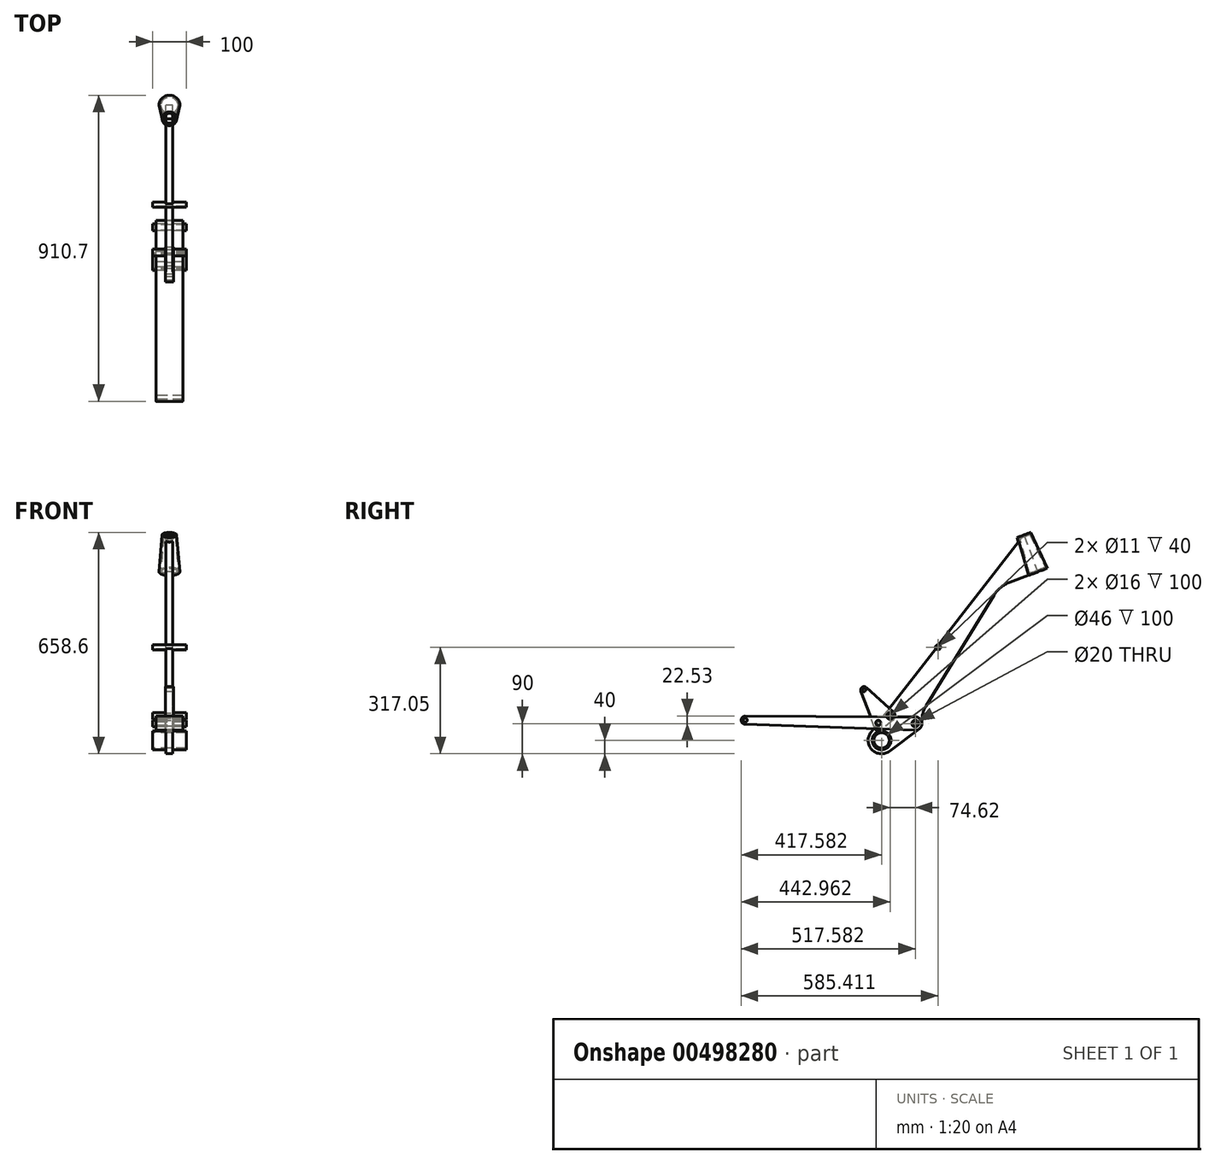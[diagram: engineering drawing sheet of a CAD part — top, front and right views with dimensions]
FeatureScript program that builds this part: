
annotation { "Feature Type Name" : "Feature", "Feature Type Description" : "" }
export const myFeature = defineFeature(function(context is Context, id is Id, definition is map)
    precondition{}
    {
        {
            var Q0;
            Q0=qCreatedBy(makeId("Right.planeOp"),FACE);
            var sketch = newSketch(context, id + "F0", { "sketchPlane" : qUnion([Q0])});
            skLineSegment(sketch, "E0", {"start": v(0, 0) * mm, "end": v(-83.68, 223.8) * mm, "construction": true});
            skLineSegment(sketch, "E1", {"start": v(-295.85, 645.65) * mm, "end": v(-16.13, -102.49) * mm, "construction": true});
            skPoint(sketch, "E2", {"position": v(-219.37, 441.1) * mm});
            skLineSegment(sketch, "E3", {"start": v(-285.85, 416.25) * mm, "end": v(-152.9, 465.96) * mm, "construction": true});
            skCircle(sketch, "E4", {"center": v(0, -8.13) * mm, "radius": 375.7 * mm, "construction": true});
            skPoint(sketch, "E5", {"position": v(-260.46, 551) * mm});
            skPoint(sketch, "E6", {"position": v(-683.46, -60) * mm});
            skPoint(sketch, "E7", {"position": v(-1089.04, 0) * mm});
            skLineSegment(sketch, "E8", {"start": v(-1089.04, 0) * mm, "end": v(0, 0) * mm, "construction": true});
            skCircle(sketch, "E9", {"center": v(-1089.04, 0) * mm, "radius": 375.7 * mm, "construction": true});
            skLineSegment(sketch, "E10", {"start": v(-683.46, -60) * mm, "end": v(-904.4, 662.68) * mm, "construction": true});
            skLineSegment(sketch, "E11", {"start": v(-260.46, 551) * mm, "end": v(-947.84, 551) * mm, "construction": true});
            skPoint(sketch, "E12", {"position": v(-870.26, 551) * mm});
            skLineSegment(sketch, "E13", {"start": v(-207.61, 570.76) * mm, "end": v(-313.3, 531.24) * mm, "construction": true});
            skPoint(sketch, "E14", {"position": v(-249.95, 522.9) * mm});
            skLineSegment(sketch, "E15", {"start": v(-683.46, -60) * mm, "end": v(-249.95, 522.9) * mm, "construction": true});
            skPoint(sketch, "E16", {"position": v(-785.79, 274.7) * mm});
            skLineSegment(sketch, "E17", {"start": v(-785.79, 274.7) * mm, "end": v(-249.95, 522.9) * mm, "construction": true});
            skPoint(sketch, "E18", {"position": v(-517.87, 398.8) * mm});
            skSolve(sketch);
        }
        {
            var Q0;
            Q0=qCreatedBy(makeId("Right.planeOp"),FACE);
            var sketch = newSketch(context, id + "F1", { "sketchPlane" : qUnion([Q0])});
            skLineSegment(sketch, "E19", {"start": v(-243.73, 432) * mm, "end": v(-245.48, 436.69) * mm});
            skLineSegment(sketch, "E20", {"start": v(-275.1, 540.19) * mm, "end": v(-245.48, 436.69) * mm});
            skLineSegment(sketch, "E21", {"start": v(-275.1, 540.19) * mm, "end": v(-276.85, 544.87) * mm});
            skLineSegment(sketch, "E22", {"start": v(-276.85, 544.87) * mm, "end": v(-280.8, 543.4) * mm});
            skLineSegment(sketch, "E23", {"start": v(-280.8, 543.4) * mm, "end": v(-248.4, 430.25) * mm});
            skLineSegment(sketch, "E24", {"start": v(-248.4, 430.25) * mm, "end": v(-243.73, 432) * mm});
            skSolve(sketch);
        }
        {
            var Q0;
            Q0=qSketchRegion(id+"F1",true);
            var Q1;
            Q1=sQuery(id+"F0.wireOp",EDGE,"E1");
            revolve(context, id + "F2", {"entities" : qUnion([Q0]), "axis" : qUnion([Q1]), "revolveType" : RevolveType.FULL});
        }
        {
            var Q0;
            Q0=qCreatedBy(makeId("Right.planeOp"),FACE);
            var sketch = newSketch(context, id + "F3", { "sketchPlane" : qUnion([Q0])});
            skCircle(sketch, "E25", {"center": v(-683.46, -60) * mm, "radius": 23 * mm});
            skCircle(sketch, "E26", {"center": v(-683.46, -60) * mm, "radius": 28 * mm});
            skSolve(sketch);
        }
        {
            var Q0;
            Q0=qSketchRegion(id+"F3",true);
            extrude(context, id + "F4", {"entities" : qUnion([Q0]), "operationType" : NewBodyOperationType.ADD, "endBound" : BoundingType.SYMMETRIC, "depth" : 100 * mm});
        }
        {
            var Q0;
            Q0=qCreatedBy(makeId("Right.planeOp"),FACE);
            var sketch = newSketch(context, id + "F5", { "sketchPlane" : qUnion([Q0])});
            skPoint(sketch, "E27", {"position": v(-583.46, -10) * mm});
            skPoint(sketch, "E28", {"position": v(-658.08, 12.53) * mm});
            skPoint(sketch, "E29", {"position": v(-515.63, 217.05) * mm});
            skSolve(sketch);
        }
        {
            var Q0;
            Q0=qCreatedBy(makeId("Right.planeOp"),FACE);
            var sketch = newSketch(context, id + "F6", { "sketchPlane" : qUnion([Q0])});
            skLineSegment(sketch, "E30", {"start": v(-715.07, -35.5) * mm, "end": v(-489.57, 255.43) * mm});
            skArc(sketch, "E31", {"start": v(-715.07, -35.5) * mm, "mid": v(-711.97, -88.06) * mm, "end": v(-659.46, -92) * mm});
            skLineSegment(sketch, "E32", {"start": v(-550.82, 43.19) * mm, "end": v(-348.97, 372.18) * mm});
            skLineSegment(sketch, "E33", {"start": v(-303.46, 409.67) * mm, "end": v(-219.37, 441.1) * mm});
            skLineSegment(sketch, "E34", {"start": v(-260.46, 551) * mm, "end": v(-219.37, 441.1) * mm});
            skArc(sketch, "E35", {"start": v(-303.46, 409.67) * mm, "mid": v(-329.35, 394.73) * mm, "end": v(-348.97, 372.18) * mm});
            skCircle(sketch, "E36", {"center": v(-683.46, -60) * mm, "radius": 28 * mm});
            skLineSegment(sketch, "E37", {"start": v(-659.46, -92) * mm, "end": v(-571.46, -26) * mm});
            skArc(sketch, "E38", {"start": v(-571.46, -26) * mm, "mid": v(-565.27, -18.31) * mm, "end": v(-563.5, -8.6) * mm});
            skArc(sketch, "E39", {"start": v(-546.3, 182.24) * mm, "mid": v(-478.96, 188.63) * mm, "end": v(-489.57, 255.43) * mm});
            skLineSegment(sketch, "E40.trimOffspring", {"start": v(-546.3, 182.24) * mm, "end": v(-260.46, 551) * mm});
            skArc(sketch, "E41", {"start": v(-550.82, 43.19) * mm, "mid": v(-561.21, 18.28) * mm, "end": v(-563.5, -8.6) * mm});
            skCircle(sketch, "E42", {"center": v(-658.08, 12.53) * mm, "radius": 10 * mm});
            skCircle(sketch, "E43", {"center": v(-583.46, -10) * mm, "radius": 10 * mm});
            skCircle(sketch, "E44", {"center": v(-515.63, 217.05) * mm, "radius": 7.5 * mm});
            skSolve(sketch);
        }
        {
            var Q0;
            Q0=qSketchRegion(id+"F6",true);
            extrude(context, id + "F7", {"entities" : qUnion([Q0]), "operationType" : NewBodyOperationType.ADD, "endBound" : BoundingType.SYMMETRIC, "depth" : 20 * mm});
        }
        {
            var Q0;
            Q0=qCreatedBy(makeId("Right.planeOp"),FACE);
            var sketch = newSketch(context, id + "F8", { "sketchPlane" : qUnion([Q0])});
            skCircle(sketch, "E45", {"center": v(-515.63, 217.05) * mm, "radius": 7.5 * mm});
            skCircle(sketch, "E46", {"center": v(-583.46, -10) * mm, "radius": 10 * mm});
            skCircle(sketch, "E47", {"center": v(-658.08, 12.53) * mm, "radius": 10 * mm});
            skCircle(sketch, "E48", {"center": v(-515.63, 217.05) * mm, "radius": 5.5 * mm});
            skCircle(sketch, "E49", {"center": v(-583.46, -10) * mm, "radius": 8 * mm});
            skCircle(sketch, "E50", {"center": v(-658.08, 12.53) * mm, "radius": 8 * mm});
            skSolve(sketch);
        }
        {
            var Q0;
            Q0 = qSketchRegion(id + "F8", true);
            extrude(context, id + "F9", {"entities" : qUnion([Q0]), "operationType" : NewBodyOperationType.ADD, "endBound" : BoundingType.SYMMETRIC, "depth" : 100 * mm});
        }
        {
            var Q0;
            Q0=qCreatedBy(makeId("Right.planeOp"),FACE);
            var sketch = newSketch(context, id + "F10", { "sketchPlane" : qUnion([Q0])});
            skLineSegment(sketch, "E51", {"start": v(-1089.47, -12) * mm, "end": v(-584.17, -29.99) * mm});
            skArc(sketch, "E52", {"start": v(-584.17, -29.99) * mm, "mid": v(-563.46, -10.4) * mm, "end": v(-583.38, 10) * mm});
            skCircle(sketch, "E53", {"center": v(-1089.04, 0) * mm, "radius": 6 * mm});
            skCircle(sketch, "E54", {"center": v(-583.46, -10) * mm, "radius": 10 * mm});
            skArc(sketch, "E55", {"start": v(-1089, 12) * mm, "mid": v(-1101.04, 0.24) * mm, "end": v(-1089.47, -12) * mm});
            skLineSegment(sketch, "E56", {"start": v(-1089, 12) * mm, "end": v(-583.38, 10) * mm});
            skCircle(sketch, "E57", {"center": v(-693.44, -7.82) * mm, "radius": 7.5 * mm});
            skSolve(sketch);
        }
        {
            var Q0;
            Q0 = qSketchRegion(id + "F10", true);
            extrude(context, id + "F11", {"entities" : qUnion([Q0]), "endBound" : BoundingType.SYMMETRIC, "depth" : 80 * mm, "offsetDistance" : 25 * mm});
        }
        {
            var Q0;
            Q0=qCreatedBy(makeId("Right.planeOp"),FACE);
            var sketch = newSketch(context, id + "F12", { "sketchPlane" : qUnion([Q0])});
            skPoint(sketch, "E58", {"position": v(-735.6, 90.05) * mm});
            skPoint(sketch, "E59", {"position": v(-693.44, -22.82) * mm});
            skLineSegment(sketch, "E60", {"start": v(-728.86, 97.44) * mm, "end": v(-647.97, 23.6) * mm});
            skLineSegment(sketch, "E61", {"start": v(-648.59, 0.91) * mm, "end": v(-687.11, -30.56) * mm});
            skLineSegment(sketch, "E62", {"start": v(-702.8, -26.32) * mm, "end": v(-744.97, 86.55) * mm});
            skArc(sketch, "E63", {"start": v(-728.86, 97.44) * mm, "mid": v(-741.2, 98.34) * mm, "end": v(-744.97, 86.55) * mm});
            skArc(sketch, "E64", {"start": v(-648.59, 0.91) * mm, "mid": v(-643.08, 12.12) * mm, "end": v(-647.97, 23.6) * mm});
            skArc(sketch, "E65", {"start": v(-702.8, -26.32) * mm, "mid": v(-696.05, -32.47) * mm, "end": v(-687.11, -30.56) * mm});
            skCircle(sketch, "E66", {"center": v(-735.6, 90.05) * mm, "radius": 5 * mm});
            skCircle(sketch, "E67", {"center": v(-693.44, -22.82) * mm, "radius": 5 * mm});
            skSolve(sketch);
        }
        {
            var Q0;
            Q0 = qSketchRegion(id + "F12", true);
            extrude(context, id + "F13", {"entities" : qUnion([Q0]), "endBound" : BoundingType.SYMMETRIC, "depth" : 25 * mm});
        }
    });
